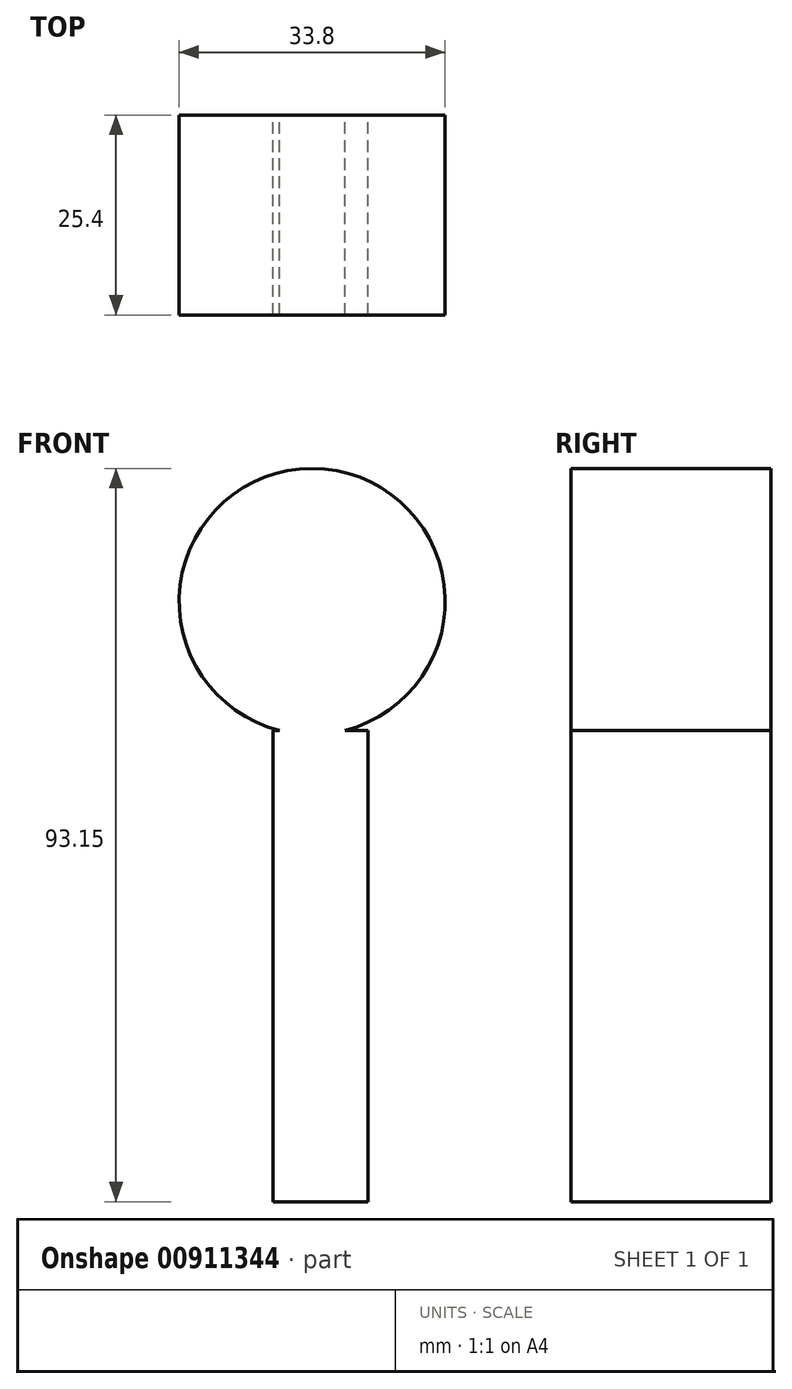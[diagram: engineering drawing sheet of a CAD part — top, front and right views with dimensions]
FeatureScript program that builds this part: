
annotation { "Feature Type Name" : "Feature", "Feature Type Description" : "" }
export const myFeature = defineFeature(function(context is Context, id is Id, definition is map)
    precondition{}
    {
        {
            var Q0;
            Q0=qCreatedBy(makeId("Front.planeOp"),FACE);
            var sketch = newSketch(context, id + "F0", { "sketchPlane" : qUnion([Q0])});
            skLineSegment(sketch, "E0.bottom", {"start": v(-4.97, 25.9) * mm, "end": v(7.11, 25.9) * mm});
            skLineSegment(sketch, "E0.top", {"start": v(-4.97, -33.96) * mm, "end": v(7.11, -33.96) * mm});
            skLineSegment(sketch, "E0.left", {"start": v(-4.97, 25.9) * mm, "end": v(-4.97, -33.96) * mm});
            skLineSegment(sketch, "E0.right", {"start": v(7.11, 25.9) * mm, "end": v(7.11, -33.96) * mm});
            skSolve(sketch);
        }
        {
            var Q0;
            Q0=makeQuery(id+"F0.imprint","IMPRINT",FACE,{"disambiguationData":[TD([[makeQuery(id+"F0.imprint","IMPRINT",EDGE,{"derivedFrom":sQuery(id+"F0.wireOp",EDGE,"E0.bottom")}),-1.0]])]});
            extrude(context, id + "F1", {"entities" : qUnion([Q0]), "depth" : 25.4 * mm, "offsetDistance" : 25.4 * mm});
        }
        {
            var Q0;
            Q0=qCreatedBy(makeId("Front.planeOp"),FACE);
            var sketch = newSketch(context, id + "F2", { "sketchPlane" : qUnion([Q0])});
            skCircle(sketch, "E1", {"center": v(0, 42.29) * mm, "radius": 16.9 * mm});
            skSolve(sketch);
        }
        {
            var Q0;
            Q0=makeQuery(id+"F2.imprint","IMPRINT",FACE,{"disambiguationData":[TD([[makeQuery(id+"F2.imprint","IMPRINT",EDGE,{"derivedFrom":sQuery(id+"F2.wireOp",EDGE,"E1")}),1.0]])]});
            extrude(context, id + "F3", {"entities" : qUnion([Q0]), "operationType" : NewBodyOperationType.ADD, "depth" : 25.4 * mm, "offsetDistance" : 25.4 * mm});
        }
    });
